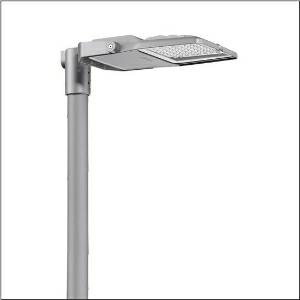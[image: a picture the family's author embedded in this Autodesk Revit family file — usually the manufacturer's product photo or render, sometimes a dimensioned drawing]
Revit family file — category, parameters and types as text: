
# Revit family: floodlight_fl_21_mini___pl61_5xa7772d4c3a_d70e
name_source: partatom
category: Lighting Fixtures
units: mm (PartAtom-declared; Revit-internal decimal feet)

## family parameters
Cut with Voids When Loaded = No
Host = Face
Light Source = No
Part Type = Normal
Room Calculation Point = No
Round Connector Dimension = Use Diameter
Shared = No

## types (1)
- --- (1 x LED, 18260 lm, 143 W, 4000K)
    Apparent Load = 143 VA
    CIE Flux Codes = 33 65 98 100 100
    Color Rendering = 70
    Color Temperature = 4000K
    Default Elevation = 1800 mm
    Description = Floodlight FL 21 mini, floodlight, primary light control with lens, of PMMA, primary optical cover: protective disc, of toughened safety glass, transparent, light distribution: PL61, light emission: direct distribution, installation type: surface-mounted, LED, High Power LED, rated luminous flux: 18.260lm, luminous efficacy: 128lm/W, light colour: 740, colour temperature: 4000K, control gear: ECG iQ, control: Auto-Match, Temp-Guard, Night-Set, Smart-Wire, Desk-Remote (wireless, voltage-free reading and setting of iQ features in the workshop via application-optimized NFC function/RFID function), optimised constant luminous flux control (CLO 2.0), Light-Fading, Lumen-Switch, with terminal, 6-pole, mains connection: 220..240V, AC, 50/60Hz, start of lifetime: 143W, end of lifetime: 152W, reduction: 61W, luminaire housing, of diecast aluminium, powder-coated, Siteco® metallic grey (DB 702S), corrosivity category C5 according to DIN EN ISO 12944, mast bracket, of steel, galvanised, powder-coated, protection rating (complete): IP66, insulation class (complete): insulation class II (safety insulation), certification: CE, ENEC, VDE, protection symbol: D, impact resistance: IK08, permissible operating ambient temperature: -40..+40°C, permissible operating ambient temperature for outdoor applications: -40..+50°C, standard: DIN EN 12944, packaging unit: 1 piece

Light Distribution: PL61
    Height = 70 mm
    Lamp = 1 x LED
    Lamp Light Flux = 18260 lm
    Lamp Power = 143 W
    Lamp count = 1
    Length = 485 mm
    Luminous efficacy = 128 lm/W
    Manufacturer = Siteco
    ModVariant = No
    Model = 5XA7772D4C3A
    Number of Poles = 1
    OnlyDefault = Yes
    Power Factor = 1
    Product Name = Floodlight FL 21 mini | PL61
    Product group = floodlight | pylon top
    ProductGroupID = 6101
    Protection Class = Protection class II
    Protection Degree = IP 66
    RLX_Detail_Level = 1
    RlxData = <blob elided: 101593 chars, md5=a46d4b99>
    Socket = socket
    Standby Power = 0 W
    System Light Flux = 18260 lm
    System Power = 143 W
    Type Comments = factory setting: luminous flux: 100 % | dim-lin: 254 | 730 mA
    Type Image = l_1007125.jpg
    URL = http://relux.com
    VarID = @adj_084625
    Voltage = 0 V
    Weight = 0.00 kg
    Width = 337 mm

## geometry (parser evidence)
native form markers: Blend x4, Sweep x13
no freeform markers — native parametric forms only
